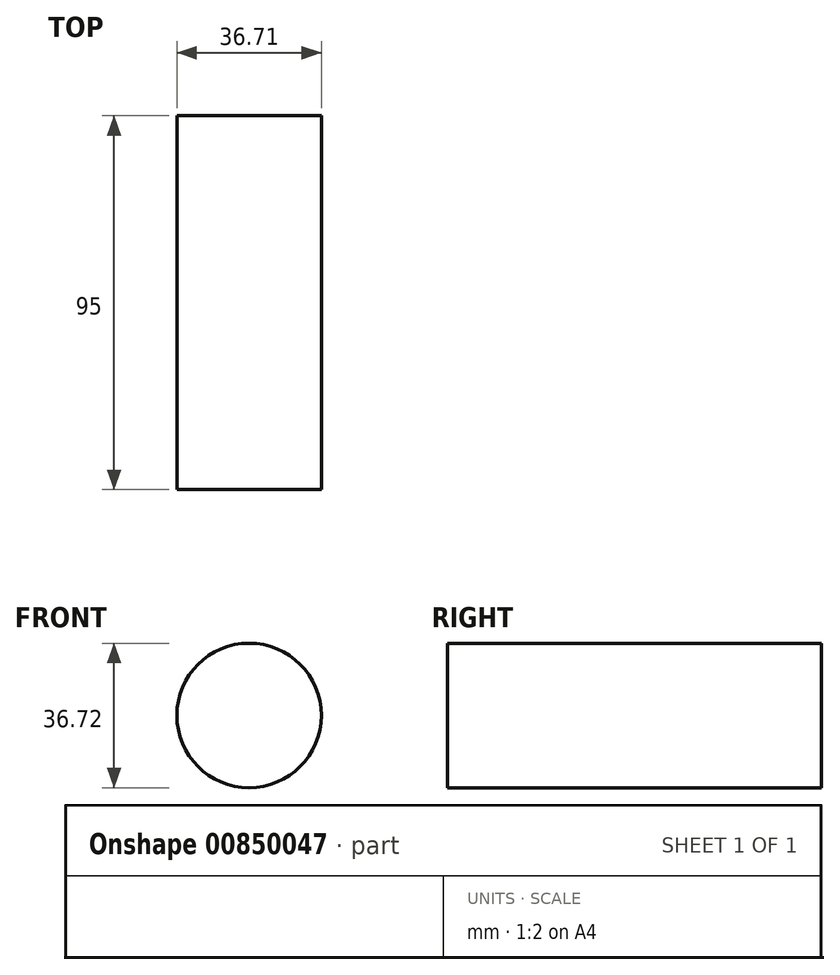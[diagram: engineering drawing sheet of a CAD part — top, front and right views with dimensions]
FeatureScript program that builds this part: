
annotation { "Feature Type Name" : "Feature", "Feature Type Description" : "" }
export const myFeature = defineFeature(function(context is Context, id is Id, definition is map)
    precondition{}
    {
        {
            var Q0;
            Q0=qCreatedBy(makeId("Front.planeOp"),FACE);
            var sketch = newSketch(context, id + "F0", { "sketchPlane" : qUnion([Q0])});
            skCircle(sketch, "E0", {"center": v(-6.13, 0) * mm, "radius": 18.36 * mm});
            skSolve(sketch);
        }
        {
            var Q0;
            Q0 = qSketchRegion(id + "F0", true);
            extrude(context, id + "F1", {"entities" : qUnion([Q0]), "depth" : 95 * mm, "offsetDistance" : 25.4 * mm});
        }
    });
